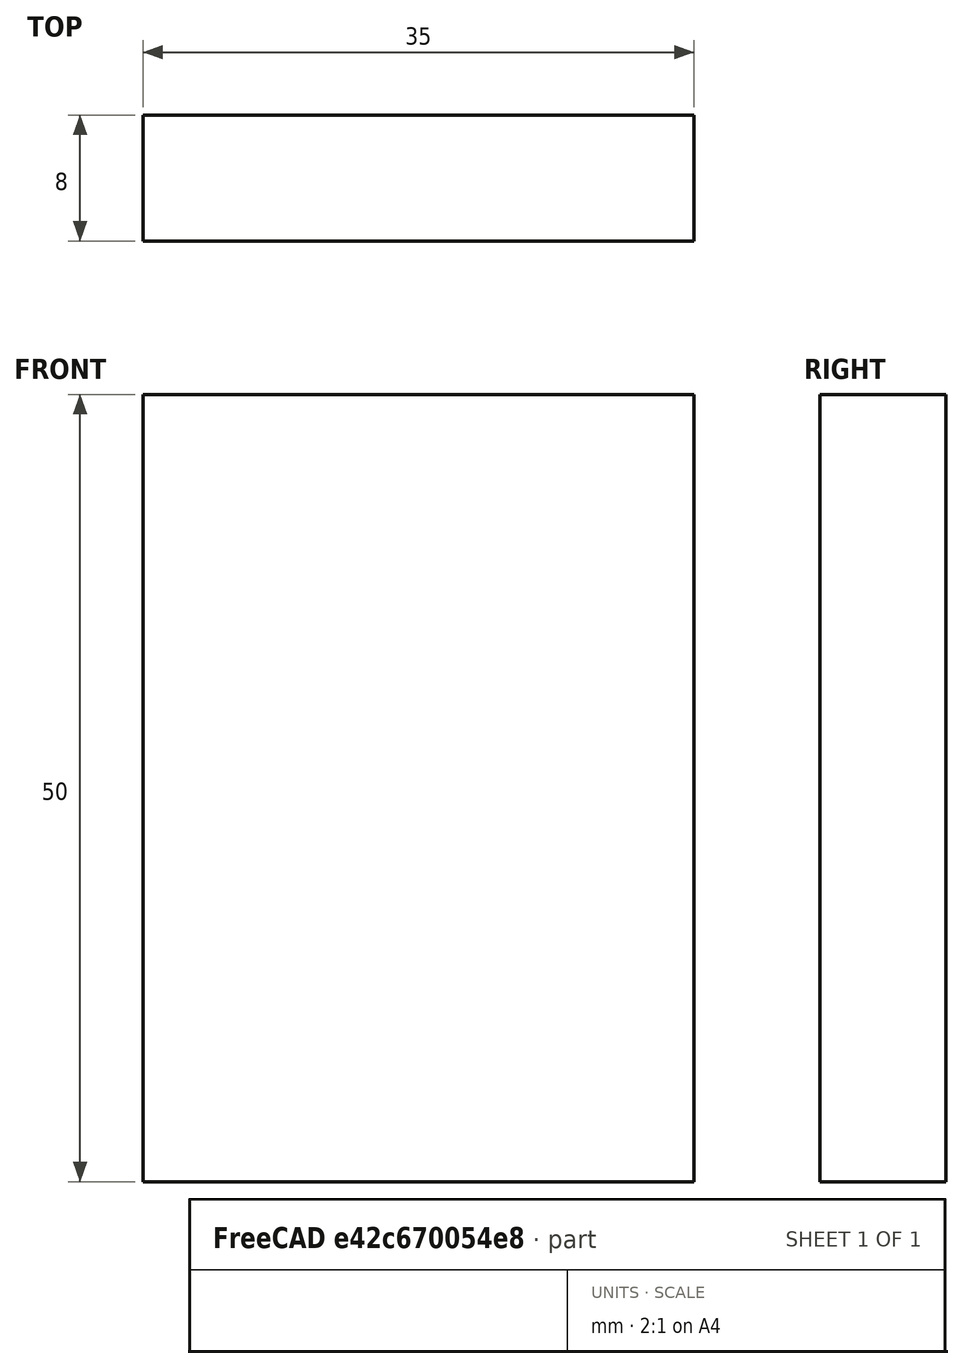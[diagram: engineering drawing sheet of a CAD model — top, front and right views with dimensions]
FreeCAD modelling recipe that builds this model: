
FCSTD DOCUMENT  (FreeCAD 0.15R4671 (Git))
Label: Flat Bar 35x8 EN10058 S235JR
License: All rights reserved
LicenseURL: http://en.wikipedia.org/wiki/All_rights_reserved
objects: Sketcher::SketchObject×1, Part::Extrusion×1
note: 2 computed .brp shape members not serialized (recipe doc carries the construction recipe); baked Part::Feature solids carry a one-line shape summary decoded from their .brp

FEATURE [Sketcher::SketchObject] Sketch
  sketch-geometry (4):
    g0: LineSegment StartX=-17.5 StartY=-4 StartZ=0 EndX=17.5 EndY=-4 EndZ=0
    g1: LineSegment StartX=17.5 StartY=-4 StartZ=0 EndX=17.5 EndY=4 EndZ=0
    g2: LineSegment StartX=17.5 StartY=4 StartZ=0 EndX=-17.5 EndY=4 EndZ=0
    g3: LineSegment StartX=-17.5 StartY=4 StartZ=0 EndX=-17.5 EndY=-4 EndZ=0
  constraints (12):
    c: Coincident(g0,g1)
    c: Coincident(g1,g2)
    c: Coincident(g2,g3)
    c: Coincident(g3,g0)
    c: Horizontal(g0)
    c: Horizontal(g2)
    c: Vertical(g1)
    c: Vertical(g3)
    c: Symmetric(g1,g2,g-2)
    c: Symmetric(g0,g1,g-1)
    c: DistanceY(g1) = 8
    c: DistanceX(g0) = 35
FEATURE [Part::Extrusion] Extrude  label="Flat Bar 35x8 EN10058 S235JR"
  Base = -> Sketch
  Dir = (0,0,50)
  Solid = true
